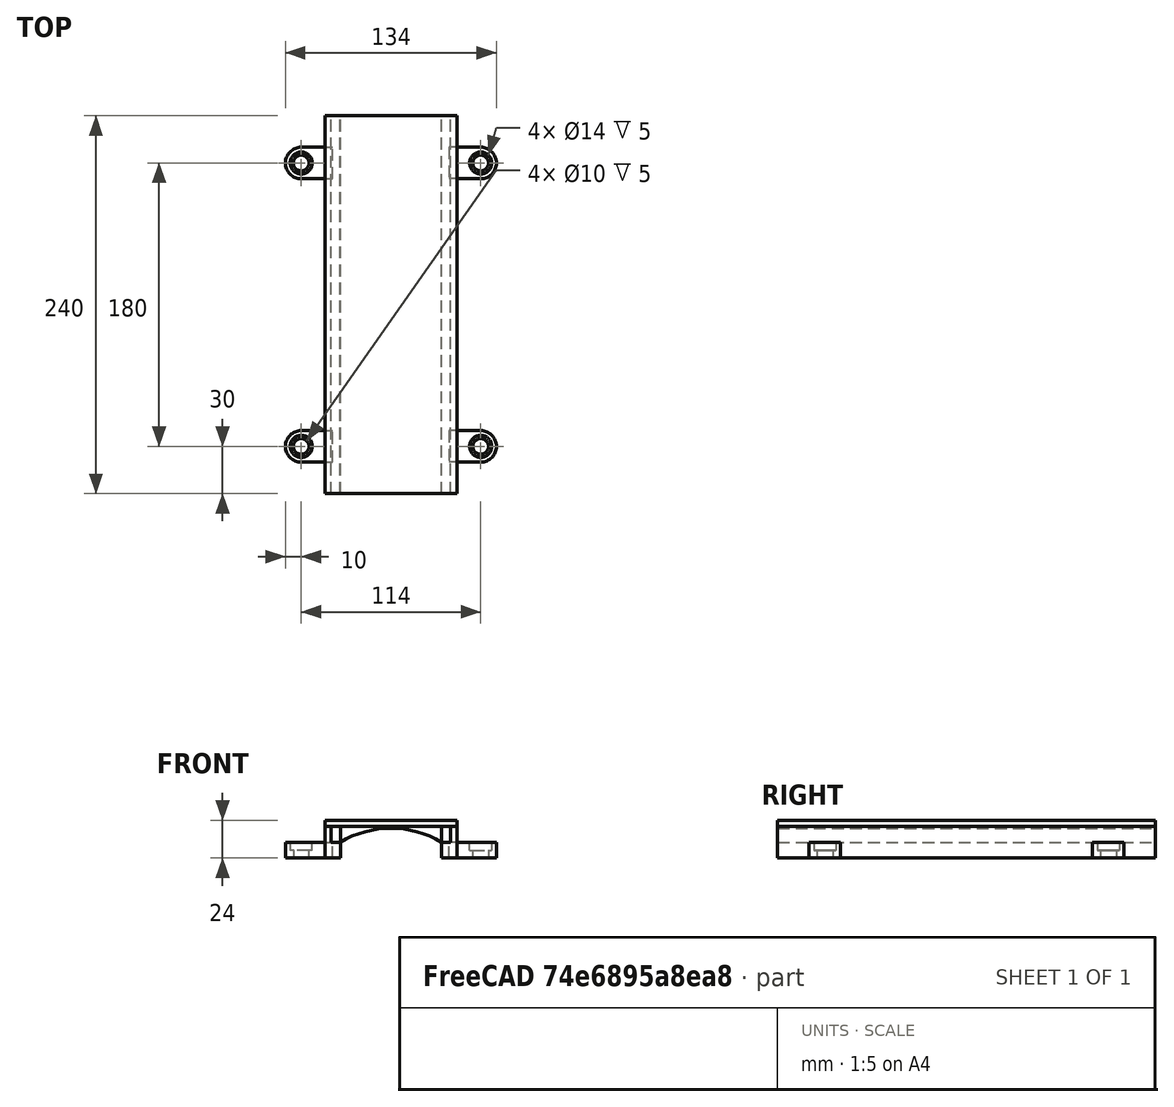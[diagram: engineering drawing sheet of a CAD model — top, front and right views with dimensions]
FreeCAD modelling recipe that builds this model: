
FCSTD DOCUMENT  (FreeCAD 1.0RUnknown)
Label: cable-management
License: All rights reserved
LicenseURL: https://en.wikipedia.org/wiki/All_rights_reserved
objects: Part::Cylinder×13, Part::Cut×9, Part::Box×8, Part::MultiFuse×4, App::DocumentObjectGroup×1
note: 34 computed .brp shape members not serialized (recipe doc carries the construction recipe); baked Part::Feature solids carry a one-line shape summary decoded from their .brp

FEATURE [Part::Cylinder] Cylinder
  Angle = 360
  AttacherType = Attacher::AttachEngine3D
  FirstAngle = 0
  Height = 10
  Placement = pos=(-19,10,-10) rot=(0,0,1;0rad)
  Radius = 10
  SecondAngle = 0
FEATURE [Part::Box] Box003  label="Cube003"
  AttacherType = Attacher::AttachEngine3D
  Height = 10
  Length = 20
  Placement = pos=(-19,0,-10) rot=(0,0,1;0rad)
  Width = 20
FEATURE [Part::Box] Box004  label="Cube004"
  AttacherType = Attacher::AttachEngine3D
  Height = 10
  Length = 76
  Width = 240
FEATURE [Part::Box] Box005  label="Cube005"
  AttacherType = Attacher::AttachEngine3D
  Height = 20
  Length = 10
  Placement = pos=(-4,0,-10) rot=(0,0,1;0rad)
  Width = 240
FEATURE [Part::Cylinder] Cylinder001
  Angle = 180
  AttacherType = Attacher::AttachEngine3D
  FirstAngle = 0
  Height = 240
  Placement = pos=(38,240,-53) rot=(-1,0,0;4.71239rad)
  Radius = 62
  SecondAngle = 0
FEATURE [Part::Cut] Cut
  Base = -> Box004
  Tool = -> Cylinder001
FEATURE [Part::Box] Box006  label="Cube006"
  AttacherType = Attacher::AttachEngine3D
  Height = 20
  Length = 10
  Placement = pos=(70,0,-10) rot=(0,0,1;0rad)
  Width = 240
FEATURE [Part::Cylinder] Cylinder002
  Angle = 360
  AttacherType = Attacher::AttachEngine3D
  FirstAngle = 0
  Height = 10
  Placement = pos=(-19,10,-5) rot=(0,0,1;0rad)
  Radius = 7
  SecondAngle = 0
FEATURE [Part::Cylinder] Cylinder003
  Angle = 360
  AttacherType = Attacher::AttachEngine3D
  FirstAngle = 0
  Height = 10
  Placement = pos=(-19,10,-10) rot=(0,0,1;0rad)
  Radius = 5
  SecondAngle = 0
FEATURE [Part::MultiFuse] Fusion  label="Mount-Point"
  Shapes = -> [Box003,Cylinder]
FEATURE [Part::Cut] Cut001
  Base = -> Fusion
  Tool = -> Cylinder002
FEATURE [Part::Cut] Cut002
  Base = -> Cut001
  Placement = pos=(0,20,0) rot=(0,0,1;0rad)
  Tool = -> Cylinder003
FEATURE [Part::Box] Box  label="Cube"
  AttacherType = Attacher::AttachEngine3D
  Height = 4
  Length = 84
  Placement = pos=(-4,0,10) rot=(0,0,1;0rad)
  Width = 240
FEATURE [App::DocumentObjectGroup] Group001  label="Base-3in"
  Group = -> [Box,Box005,Box006,Cut]
FEATURE [Part::Box] Box007  label="Cube007"
  AttacherType = Attacher::AttachEngine3D
  Height = 10
  Length = 20
  Placement = pos=(-19,0,-10) rot=(0,0,1;0rad)
  Width = 20
FEATURE [Part::Cylinder] Cylinder004
  Angle = 360
  AttacherType = Attacher::AttachEngine3D
  FirstAngle = 0
  Height = 10
  Placement = pos=(-19,10,-10) rot=(0,0,1;0rad)
  Radius = 10
  SecondAngle = 0
FEATURE [Part::Cylinder] Cylinder005
  Angle = 360
  AttacherType = Attacher::AttachEngine3D
  FirstAngle = 0
  Height = 10
  Placement = pos=(-19,10,-5) rot=(0,0,1;0rad)
  Radius = 7
  SecondAngle = 0
FEATURE [Part::Cylinder] Cylinder006
  Angle = 360
  AttacherType = Attacher::AttachEngine3D
  FirstAngle = 0
  Height = 10
  Placement = pos=(-19,10,-10) rot=(0,0,1;0rad)
  Radius = 5
  SecondAngle = 0
FEATURE [Part::MultiFuse] Fusion001  label="Mount-Point001"
  Shapes = -> [Box007,Cylinder004]
FEATURE [Part::Cut] Cut003
  Base = -> Fusion001
  Tool = -> Cylinder005
FEATURE [Part::Cut] Cut004
  Base = -> Cut003
  Placement = pos=(76,40,0) rot=(0,0,1;3.14159rad)
  Tool = -> Cylinder006
FEATURE [Part::Box] Box008  label="Cube008"
  AttacherType = Attacher::AttachEngine3D
  Height = 10
  Length = 20
  Placement = pos=(-19,0,-10) rot=(0,0,1;0rad)
  Width = 20
FEATURE [Part::Cylinder] Cylinder007
  Angle = 360
  AttacherType = Attacher::AttachEngine3D
  FirstAngle = 0
  Height = 10
  Placement = pos=(-19,10,-10) rot=(0,0,1;0rad)
  Radius = 10
  SecondAngle = 0
FEATURE [Part::Cylinder] Cylinder008
  Angle = 360
  AttacherType = Attacher::AttachEngine3D
  FirstAngle = 0
  Height = 10
  Placement = pos=(-19,10,-5) rot=(0,0,1;0rad)
  Radius = 7
  SecondAngle = 0
FEATURE [Part::Cylinder] Cylinder009
  Angle = 360
  AttacherType = Attacher::AttachEngine3D
  FirstAngle = 0
  Height = 10
  Placement = pos=(-19,10,-10) rot=(0,0,1;0rad)
  Radius = 5
  SecondAngle = 0
FEATURE [Part::MultiFuse] Fusion002  label="Mount-Point002"
  Shapes = -> [Box008,Cylinder007]
FEATURE [Part::Cut] Cut005
  Base = -> Fusion002
  Tool = -> Cylinder008
FEATURE [Part::Cut] Cut006
  Base = -> Cut005
  Placement = pos=(0,200,0) rot=(0,0,1;0rad)
  Tool = -> Cylinder009
FEATURE [Part::Box] Box009  label="Cube009"
  AttacherType = Attacher::AttachEngine3D
  Height = 10
  Length = 20
  Placement = pos=(-19,0,-10) rot=(0,0,1;0rad)
  Width = 20
FEATURE [Part::Cylinder] Cylinder010
  Angle = 360
  AttacherType = Attacher::AttachEngine3D
  FirstAngle = 0
  Height = 10
  Placement = pos=(-19,10,-10) rot=(0,0,1;0rad)
  Radius = 10
  SecondAngle = 0
FEATURE [Part::Cylinder] Cylinder011
  Angle = 360
  AttacherType = Attacher::AttachEngine3D
  FirstAngle = 0
  Height = 10
  Placement = pos=(-19,10,-5) rot=(0,0,1;0rad)
  Radius = 7
  SecondAngle = 0
FEATURE [Part::Cylinder] Cylinder012
  Angle = 360
  AttacherType = Attacher::AttachEngine3D
  FirstAngle = 0
  Height = 10
  Placement = pos=(-19,10,-10) rot=(0,0,1;0rad)
  Radius = 5
  SecondAngle = 0
FEATURE [Part::MultiFuse] Fusion003  label="Mount-Point003"
  Shapes = -> [Box009,Cylinder010]
FEATURE [Part::Cut] Cut007
  Base = -> Fusion003
  Tool = -> Cylinder011
FEATURE [Part::Cut] Cut008
  Base = -> Cut007
  Placement = pos=(76,220,0) rot=(0,0,1;3.14159rad)
  Tool = -> Cylinder012
